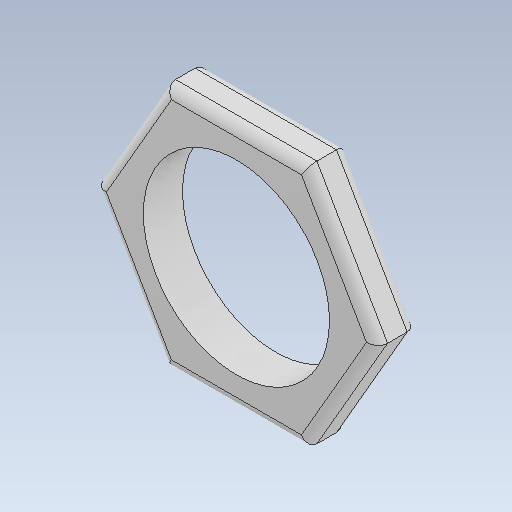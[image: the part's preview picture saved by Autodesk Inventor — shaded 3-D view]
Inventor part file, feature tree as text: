
AUTODESK INVENTOR PART (.ipt)
format: ipt  version: 2020 (Build 240168000, 168)  size: 116,736 bytes
history: native  units: in
note: dims shown in document units (in); Inventor stores cm internally (conversion verified against a paired STEP export)
features: fillet x1
ambient origin geometry x8: Origin, YZ Plane, XZ Plane, XY Plane, X Axis, Y Axis, Z Axis, Center Point
bodies: Solid1 (feature_tree)
feature tree (1):
  fillet  "Fillet1"  [1 undecoded]
note: 1 required parameter value undecoded (feature->parameter linkage not recoverable at this tier; creation-order binding heuristic only, values carry confidence <= 0.55)
